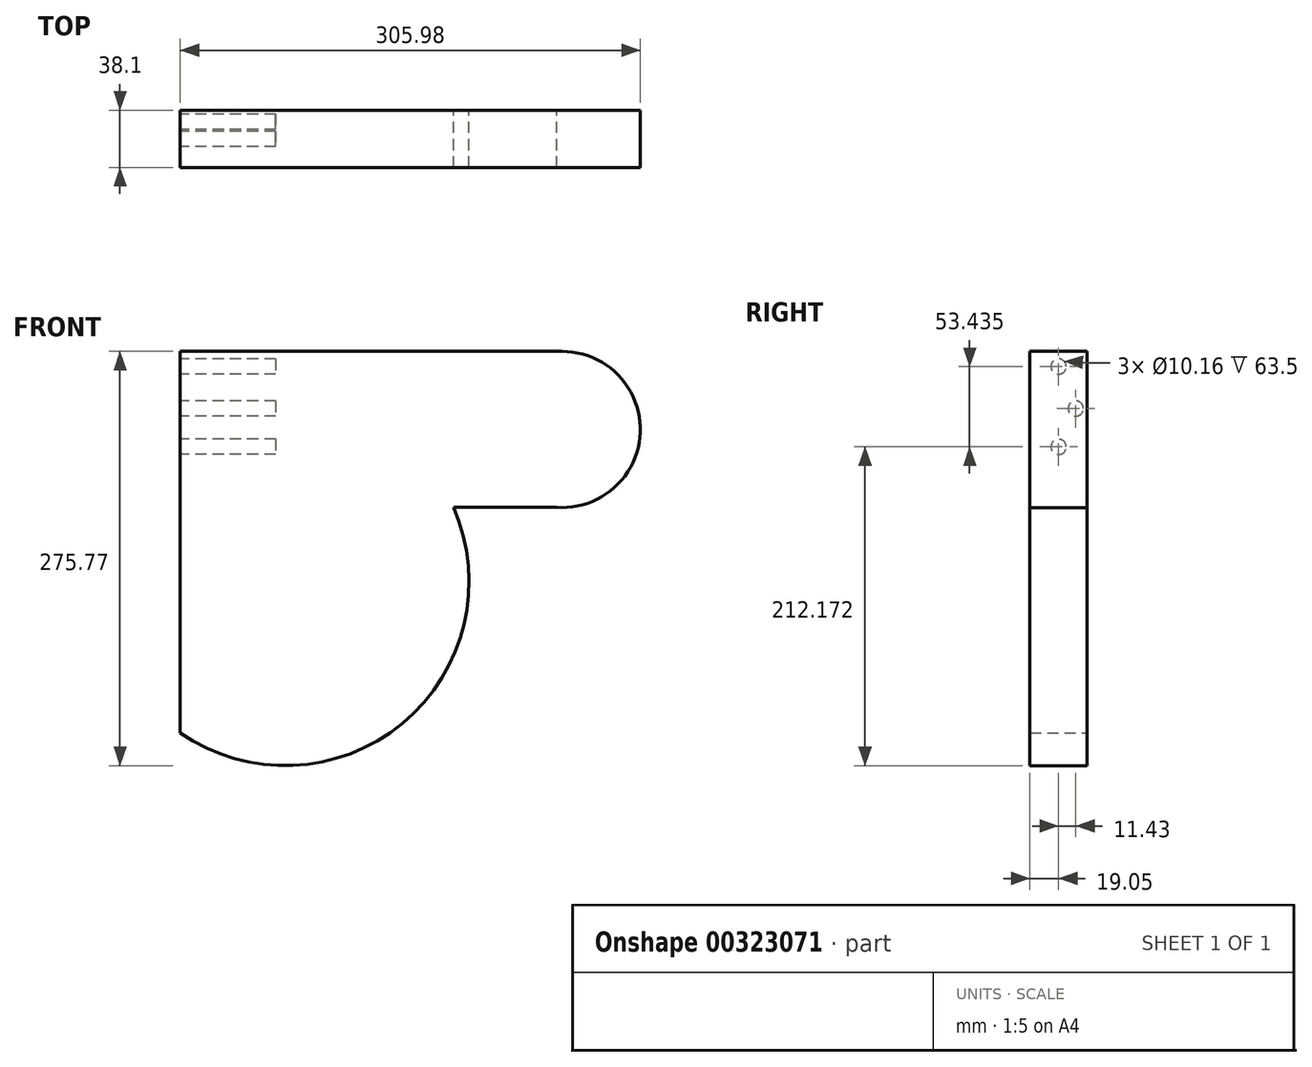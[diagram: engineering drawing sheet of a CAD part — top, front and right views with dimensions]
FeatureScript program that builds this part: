
annotation { "Feature Type Name" : "Feature", "Feature Type Description" : "" }
export const myFeature = defineFeature(function(context is Context, id is Id, definition is map)
    precondition{}
    {
        {
            var Q0;
            Q0=qCreatedBy(makeId("Front.planeOp"),FACE);
            var sketch = newSketch(context, id + "F0", { "sketchPlane" : qUnion([Q0])});
            skLineSegment(sketch, "E0", {"start": v(0, -150.17) * mm, "end": v(0, 103.83) * mm});
            skLineSegment(sketch, "E1", {"start": v(0, 103.83) * mm, "end": v(254, 103.83) * mm});
            skArc(sketch, "E2", {"start": v(254, 103.83) * mm, "mid": v(305.95, 49.98) * mm, "end": v(250.28, 0) * mm});
            skLineSegment(sketch, "E3", {"start": v(250.28, 0) * mm, "end": v(181.7, 0) * mm});
            skArc(sketch, "E4", {"start": v(0, -150.17) * mm, "mid": v(147.7, -143.88) * mm, "end": v(181.7, 0) * mm});
            skSolve(sketch);
        }
        {
            var Q0;
            Q0 = qSketchRegion(id + "F0", true);
            extrude(context, id + "F1", {"entities" : qUnion([Q0]), "depth" : 38.1 * mm});
        }
        {
            var Q0;
            Q0=makeQuery(id+"F1.opExtrude","SWEPT_FACE",FACE,{"disambiguationData":[OSD([sQuery(id+"F0.wireOp",EDGE,"E0")])]});
            var sketch = newSketch(context, id + "F2", { "sketchPlane" : qUnion([Q0])});
            skSolve(sketch);
        }
        {
            var Q0;
            {var subQ0=sQuery(id+"F0.wireOp",EDGE,"E0");Q0=makeQuery(id+"F2.imprint","IMPRINT",FACE,{"disambiguationData":[TD([[makeQuery(id+"F2.imprint","IMPRINT",EDGE,{"derivedFrom":makeQuery(id+"F1.opExtrude","CAP_EDGE",EDGE,{"disambiguationData":[OSD([subQ0])],"isStart":true})}),-1.0]])]});}
            var sketch = newSketch(context, id + "F3", { "sketchPlane" : qUnion([Q0])});
            skCircle(sketch, "E5", {"center": v(19.05, 93.67) * mm, "radius": 5.08 * mm});
            skCircle(sketch, "E6", {"center": v(7.62, 65.73) * mm, "radius": 5.08 * mm});
            skCircle(sketch, "E7", {"center": v(19.05, 40.23) * mm, "radius": 5.08 * mm});
            skSolve(sketch);
        }
        {
            var Q0;
            Q0 = qSketchRegion(id + "F3", true);
            extrude(context, id + "F4", {"entities" : qUnion([Q0]), "operationType" : NewBodyOperationType.REMOVE, "oppositeDirection" : true, "depth" : 63.5 * mm});
        }
    });
